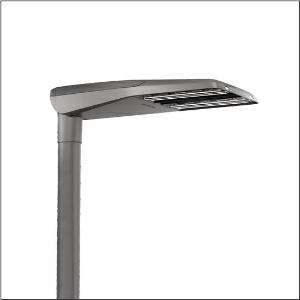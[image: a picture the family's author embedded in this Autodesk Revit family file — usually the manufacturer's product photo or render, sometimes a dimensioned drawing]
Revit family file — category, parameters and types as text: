
# Revit family: streetlight_sl_11_iq_midi___st1_2p1_0_5xc3g51e08me_ff57
name_source: partatom
category: Lighting Fixtures
units: mm (PartAtom-declared; Revit-internal decimal feet)

## family parameters
Cut with Voids When Loaded = No
Host = Face
Light Source = No
Part Type = Normal
Room Calculation Point = No
Round Connector Dimension = Use Diameter
Shared = No

## types (1)
- --- (1 x LED, 17750 lm, 124.7 W, 3000K)
    Apparent Load = 125 VA
    CIE Flux Codes = 31 68 95 100 100
    Color Rendering = 70
    Color Temperature = 3000K
    Default Elevation = 1800 mm
    Description = Streetlight SL 11 iQ midi, mast luminaire, primary light control with 3 zone facetted reflector, of plastic, silver coated, highly specular, primary optical cover: cover, of PMMA, transparent, light distribution: ST1.2P1.0, light emission: direct distribution, primary light characteristic: asymmetric, installation type: post-top, side-entry, LED, High Power LED, rated luminous flux: 17.750lm, luminous efficacy: 142lm/W, light colour: 730, colour temperature: 3000K, control: optimised constant luminous flux control (CLO 2.0), Desk-Remote (wireless, voltage-free reading and setting of iQ features in the workshop via application-optimized NFC function/RFID function), Light-Fading, Smart-Wire, Night-Set, Lumen-Switch, Temp-Guard, Auto-Match, with cable H07RN-F 5x 1.5mm², mains connection: 230..240V, AC, 50/60Hz, connection cable pre-assembled, cable length: 12,5m, start of lifetime: 125W, end of service life: 132W, reduction: 57W, luminaire housing, of diecast aluminium, powder-coated, Siteco® metallic grey (DB 702S), please order mast flange separately, inclination adjustable without tools: 0°, 5°, 10°, 15° (post-top) | 0°, -5°, -10°, -15° (side-entry), sealing non-destructively replaceable, multi-level sealing system, length: 780mm, width: 376mm, height: 118mm, mast flange for spigot size: 42mm (side-entry): 5XC10008XM4, 60/48mm (side-entry/post-top): 5XC10108XM2, 76/60mm (side-entry/post-top): 5XC10108XM1, equipment: Power, protection rating (complete): IP66, insulation class (complete): insulation class II (safety insulation), certification: CE, ENEC, VDE, impact resistance: IK09, permissible operating ambient temperature for outdoor applications: -25..+50°C, standard-compliant lighting for roads and squares, Environmental Product Declaration (EPD) tested and certified by an independent institute, packaging unit: 1 piece

Light Distribution: ST1.2P1.0
    Height = 118 mm
    Lamp = 1 x LED
    Lamp Light Flux = 17750 lm
    Lamp Power = 124.7 W
    Lamp count = 1
    Length = 780 mm
    Luminous efficacy = 142 lm/W
    Manufacturer = Siteco
    ModVariant = No
    Model = 5XC3G51E08ME
    Number of Poles = 1
    OnlyDefault = Yes
    Power Factor = 1
    Product Name = Streetlight SL 11 iQ midi | ST1.2P1.0
    Product group = mast luminaire | pylon top
    ProductGroupID = 6100
    Protection Class = Protection class II
    Protection Degree = IP 66
    RLX_Detail_Level = 1
    RLX_Emergency_Light_Flux = 0 lm
    RLX_Emergency_Type = 0
    RLX_Emergency_Type_DB = No
    RlxData = <blob elided: 70713 chars, md5=521d117b>
    Socket = socket
    Standby Power = 0 W
    System Light Flux = 17750 lm
    System Power = 125 W
    Type Comments = factory setting: luminous flux: 100 % | dim-lin: 254 | 557 mA
    Type Image = l_1005960.jpg
    URL = http://relux.com
    VarID = @adj_147541
    Voltage = 0 V
    Weight = 0.00 kg
    Width = 376 mm

## geometry (parser evidence)
native form markers: Blend x4, Sweep x12
no freeform markers — native parametric forms only
